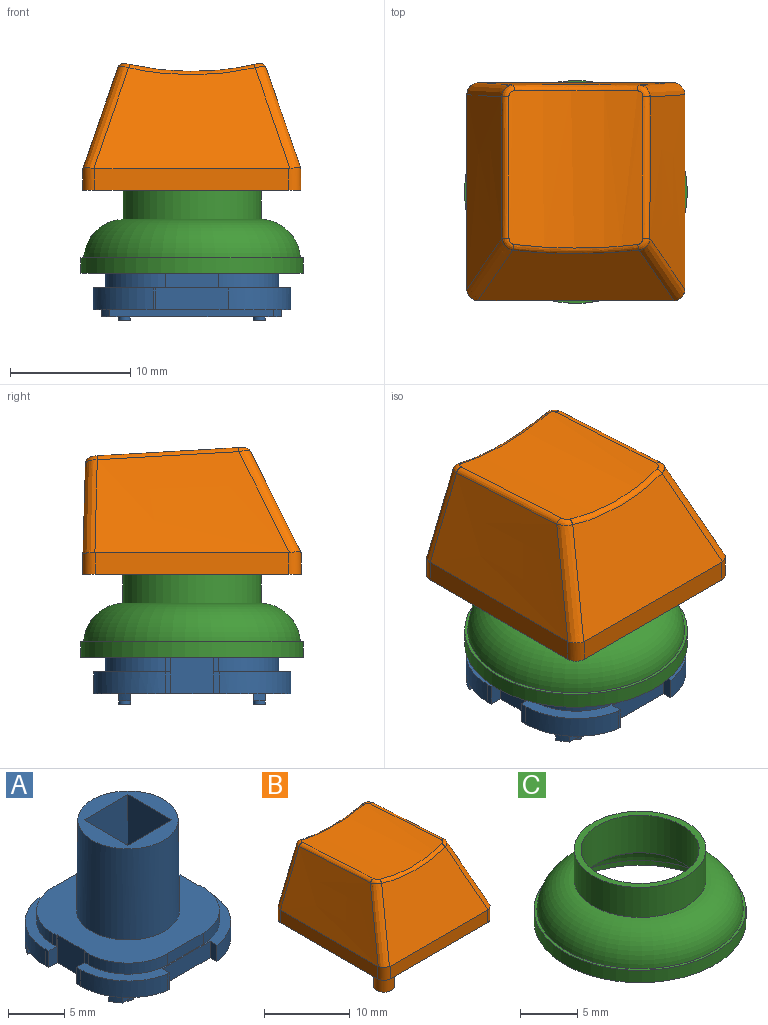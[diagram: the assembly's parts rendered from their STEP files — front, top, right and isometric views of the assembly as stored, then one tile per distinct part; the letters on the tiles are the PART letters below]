
ASSEMBLY  parts=3 mates=2
PART A: 86 faces, bbox 16.4x16.4x13.7 mm
  f0: plane 6x1.8mm, normal (0,1,0), area 10.8mm2, adj f3,f10,f11,f12
  f1: plane 1x1mm, normal (0,0,-1), area 0.8mm2, adj f13
  f2: plane 1x1mm, normal (0,0,-1), area 0.8mm2, adj f14
  f3: plane 1.8x0.85mm, normal (1,0,0), area 1.5mm2, adj f0,f11,f12,f26
  f4: plane 1.2x0.45mm, normal (-1,0,0), area 0.5mm2, adj f5,f11,f27,f28
  f5: revolved ~5x5mm, area 9.4mm2, adj f4,f6,f11,f28
  f6: plane 4.4x1.2mm, normal (0,1,0), area 5.3mm2, adj f5,f7,f11,f28
  f7: revolved ~5x5mm, area 9.4mm2, adj f6,f9,f11,f28
  f8: revolved ~9.8x9.13mm, area 277.6mm2, adj f19,f28
  f9: plane 1.2x0.45mm, normal (1,0,0), area 0.5mm2, adj f7,f11,f28,f29
  f10: plane 1.8x0.85mm, normal (-1,0,0), area 1.5mm2, adj f0,f11,f12,f31
  f11: plane 16.4x6.4mm, normal (0,0,1), area 17.2mm2, adj f0,f3,f4,f5,f6,f7,f9,f10
  f12: plane 13.52x2.05mm, normal (0,0,-1), area 17.2mm2, adj f0,f3,f10,f15,f26,f31
  f13: revolved ~1x1mm, area 0.9mm2, adj f1,f32,f33
  f14: revolved ~1x1mm, area 0.9mm2, adj f2,f33,f34
  f15: plane 13.52x0.6mm, normal (0,1,0), area 8.1mm2, adj f12,f32,f33,f34,f35,f36
  f16: plane 2.8x0.75mm, normal (0,0,-1), area 2.1mm2, adj f40,f41,f42,f43
  f17: plane 2.8x0.75mm, normal (0,0,-1), area 2.1mm2, adj f44,f45,f46,f47
  f18: plane 2.8x0.75mm, normal (0,0,-1), area 2.1mm2, adj f48,f49,f50,f51
  f19: plane 8.9x8.9mm, normal (0,0,1), area 32mm2, adj f8,f43,f47,f51,f52
  f20: plane 2.8x0.75mm, normal (0,0,-1), area 2.1mm2, adj f37,f38,f39,f52
  f21: revolved ~5x5mm, area 9.4mm2, adj f22,f24,f28,f55
  f22: plane 4.4x1.2mm, normal (0,-1,0), area 5.3mm2, adj f21,f23,f28,f55
  f23: revolved ~5x5mm, area 9.4mm2, adj f22,f28,f53,f55
  f24: plane 1.2x0.45mm, normal (1,0,0), area 0.5mm2, adj f21,f28,f55,f57
  f25: plane 1.8x0.45mm, normal (-1,0,0), area 0.8mm2, adj f11,f26,f27,f58
  f26: revolved ~5.95x5.2mm, area 15.5mm2, adj f3,f11,f12,f25,f35,f58
  f27: plane 3x1.1mm, normal (0,-1,0), area 2.1mm2, adj f4,f11,f25,f28,f58,f59,f72
  f28: plane 14.4x14.4mm, normal (0,0,1), area 119.7mm2, adj f4,f5,f6,f7,f8,f9,f21,f22
  f29: plane 3x1.1mm, normal (0,-1,0), area 2.1mm2, adj f9,f11,f28,f30,f60,f61,f72
  f30: plane 1.8x0.45mm, normal (1,0,0), area 0.8mm2, adj f11,f29,f31,f61
  f31: revolved ~5.95x5.2mm, area 15.5mm2, adj f10,f11,f12,f30,f36,f61
  f32: plane 1.86x1mm, normal (0,0,-1), area 1.1mm2, adj f13,f15,f36,f62
  f33: plane 11.2x1mm, normal (0,0,-1), area 10.4mm2, adj f13,f14,f15,f62
  f34: plane 1.85x1mm, normal (0,0,-1), area 1.1mm2, adj f14,f15,f35,f62
  f35: revolved ~1x0.69mm, area 0.7mm2, adj f15,f26,f34,f62
  f36: revolved ~1x0.69mm, area 0.7mm2, adj f15,f31,f32,f62
  f37: plane 5.9x0.75mm, normal (0,1,0), area 4.4mm2, adj f20,f38,f52,f63
  f38: plane 5.9x2.8mm, normal (1,0,0), area 16.5mm2, adj f20,f37,f39,f63
  f39: plane 5.9x0.75mm, normal (0,-1,0), area 4.4mm2, adj f20,f38,f52,f63
  f40: plane 5.9x0.75mm, normal (1,0,0), area 4.4mm2, adj f16,f41,f43,f63
  f41: plane 5.9x2.8mm, normal (0,-1,0), area 16.5mm2, adj f16,f40,f42,f63
  f42: plane 5.9x0.75mm, normal (-1,0,0), area 4.4mm2, adj f16,f41,f43,f63
  f43: plane 12.8x5.5mm, normal (0,-1,0), area 53.9mm2, adj f16,f19,f40,f42,f47,f52,f63
  f44: plane 5.9x0.75mm, normal (0,-1,0), area 4.4mm2, adj f17,f45,f47,f63
  f45: plane 5.9x2.8mm, normal (-1,0,0), area 16.5mm2, adj f17,f44,f46,f63
  f46: plane 5.9x0.75mm, normal (0,1,0), area 4.4mm2, adj f17,f45,f47,f63
  f47: plane 12.8x5.5mm, normal (-1,0,0), area 53.9mm2, adj f17,f19,f43,f44,f46,f51,f63
  f48: plane 5.9x0.75mm, normal (-1,0,0), area 4.4mm2, adj f18,f49,f51,f63
  f49: plane 5.9x2.8mm, normal (0,1,0), area 16.5mm2, adj f18,f48,f50,f63
  f50: plane 5.9x0.75mm, normal (1,0,0), area 4.4mm2, adj f18,f49,f51,f63
  f51: plane 12.8x5.5mm, normal (0,1,0), area 53.9mm2, adj f18,f19,f47,f48,f50,f52,f63
  f52: plane 12.8x5.5mm, normal (1,0,0), area 53.9mm2, adj f19,f20,f37,f39,f43,f51,f63
  f53: plane 1.2x0.45mm, normal (-1,0,0), area 0.5mm2, adj f23,f28,f55,f64
  f54: plane 1.8x0.2mm, normal (0,-1,0), area 0.4mm2, adj f55,f66,f70,f77
  f55: plane 16.4x6.45mm, normal (0,0,1), area 17.6mm2, adj f21,f22,f23,f24,f53,f54,f56,f57
  f56: plane 1.8x0.45mm, normal (1,0,0), area 0.8mm2, adj f55,f57,f69,f71
  f57: plane 3x1.1mm, normal (0,1,0), area 2.1mm2, adj f24,f28,f55,f56,f60,f71,f72
  f58: plane 3.35x1.93mm, normal (0,0,-1), area 3.5mm2, adj f25,f26,f27,f62,f72
  f59: plane 3.5x3mm, normal (-1,0,0), area 10.5mm2, adj f27,f28,f64,f72
  f60: plane 3.5x3mm, normal (1,0,0), area 10.5mm2, adj f28,f29,f57,f72
  f61: plane 3.35x1.93mm, normal (0,0,-1), area 3.5mm2, adj f29,f30,f31,f62,f72
  f62: plane 14.91x0.6mm, normal (0,-1,0), area 8.9mm2, adj f32,f33,f34,f35,f36,f58,f61,f72
  f63: plane 9.2x9.2mm, normal (0,0,-1), area 27.8mm2, adj f37,f38,f39,f40,f41,f42,f43,f44
  f64: plane 3x1.1mm, normal (0,1,0), area 2.1mm2, adj f28,f53,f55,f59,f65,f72,f73
  f65: plane 1.8x0.53mm, normal (-1,0,0), area 1mm2, adj f55,f64,f70,f73
  f66: plane 1.8x0.9mm, normal (1,0,0), area 1.6mm2, adj f54,f55,f67,f77
  f67: plane 6x1.8mm, normal (0,-1,0), area 10.8mm2, adj f55,f66,f68,f77
  f68: plane 1.8x0.85mm, normal (-1,0,0), area 1.5mm2, adj f55,f67,f69,f77
  f69: revolved ~5.95x5.2mm, area 15.5mm2, adj f55,f56,f68,f71,f75,f77
  f70: revolved ~5.92x5mm, area 15.2mm2, adj f54,f55,f65,f73,f77,f78
  f71: plane 3.35x1.93mm, normal (0,0,-1), area 3.5mm2, adj f56,f57,f69,f72,f79
  f72: plane 14.4x10.2mm, normal (0,0,-1), area 76.3mm2, adj f27,f29,f57,f58,f59,f60,f61,f62
  f73: plane 3.35x1.93mm, normal (0,0,-1), area 3.6mm2, adj f64,f65,f70,f72,f79
  f74: plane 1x1mm, normal (0,0,-1), area 0.8mm2, adj f80
  f75: revolved ~1x0.69mm, area 0.7mm2, adj f69,f76,f79,f81
  f76: plane 1.86x1mm, normal (0,0,-1), area 1.1mm2, adj f75,f79,f80,f81
  f77: plane 13.59x2.1mm, normal (0,0,-1), area 17.5mm2, adj f54,f66,f67,f68,f69,f70,f81
  f78: revolved ~1x0.67mm, area 0.7mm2, adj f70,f79,f81,f82
  f79: plane 14.95x0.6mm, normal (0,1,0), area 9mm2, adj f71,f72,f73,f75,f76,f78,f82,f83
  f80: revolved ~1x1mm, area 0.9mm2, adj f74,f76,f83
  f81: plane 13.59x0.6mm, normal (0,-1,0), area 8.2mm2, adj f75,f76,f77,f78,f82,f83
  f82: plane 1.9x1mm, normal (0,0,-1), area 1.2mm2, adj f78,f79,f81,f84
  f83: plane 11.2x1mm, normal (0,0,-1), area 10.4mm2, adj f79,f80,f81,f84
  f84: revolved ~1x1mm, area 0.9mm2, adj f82,f83,f85
  f85: plane 1x1mm, normal (0,0,-1), area 0.8mm2, adj f84
PART B: 42 faces, bbox 21.7x23.1x23.9 mm
  f0: plane 18.1x18.1mm, normal (0,0,-1), area 67.5mm2, adj f1,f2,f3,f4,f10,f12,f14,f16
  f1: plane 16.1x1.8mm, normal (1,0,0), area 29mm2, adj f0,f8,f10,f16
  f2: plane 16.11x1.81mm, normal (0,1,0), area 29mm2, adj f0,f5,f14,f15,f16,f17
  f3: plane 16.1x1.8mm, normal (-1,0,0), area 29mm2, adj f0,f6,f12,f14
  f4: plane 16.1x1.8mm, normal (0,-1,0), area 29mm2, adj f0,f7,f10,f12
  f5: plane 15.98x7.41mm, normal (0,1,0.03), area 93.8mm2, adj f2,f15,f17,f20
  f6: bspline ~18.1x8.87mm, area 120mm2, adj f3,f12,f13,f14,f15,f19
  f7: plane 16.29x8.38mm, normal (0,-0.89,0.45), area 120.9mm2, adj f4,f10,f11,f12,f13,f23
  f8: bspline ~18.1x8.87mm, area 120mm2, adj f1,f10,f11,f16,f17,f24
  f9: cylinder r=22.9mm len=12.8mm, axis (0,1,-0.06), area 143.2mm2, adj f18,f19,f20,f21,f22,f23,f24,f25
  f10: cylinder r=1mm len=1.87mm, axis (0,0,-1), area 2.9mm2, adj f0,f1,f4,f7,f8,f11
  f11: bspline ~10.73x6.1mm, area 14mm2, adj f7,f8,f10,f25
  f12: cylinder r=1mm len=1.87mm, axis (0,0,1), area 2.9mm2, adj f0,f3,f4,f6,f7,f13
  f13: bspline ~10.73x6.1mm, area 14mm2, adj f6,f7,f12,f21
  f14: cylinder r=1mm len=1.8mm, axis (0,0,-1), area 2.8mm2, adj f0,f2,f3,f6,f15
  f15: bspline ~12.92x5.65mm, area 12.7mm2, adj f2,f5,f6,f14,f18
  f16: cylinder r=1mm len=1.8mm, axis (0,0,1), area 2.8mm2, adj f0,f1,f2,f8,f17
  f17: bspline ~12.92x5.65mm, area 12.7mm2, adj f2,f5,f8,f16,f22
  f18: bspline ~1.21x1.1mm, area 0.9mm2, adj f9,f15,f19,f20
  f19: bspline ~18.69x1.5mm, area 8.7mm2, adj f6,f9,f18,f21
  f20: bspline ~10.43x1.06mm, area 7.7mm2, adj f5,f9,f18,f22
  f21: bspline ~1.16x1.07mm, area 0.7mm2, adj f9,f13,f19,f23
  f22: bspline ~1.26x1.04mm, area 0.9mm2, adj f9,f17,f20,f24
  f23: bspline ~10.5x0.84mm, area 6.1mm2, adj f7,f9,f21,f25
  f24: bspline ~18.69x1.5mm, area 8.7mm2, adj f8,f9,f22,f25
  f25: bspline ~1.25x1.04mm, area 0.7mm2, adj f9,f11,f23,f24
  f26: plane 16.11x1.64mm, normal (-1,0,0), area 26.2mm2, adj f0,f27,f29,f32,f33
  f27: plane 16.1x1.79mm, normal (0,-1,0), area 28.7mm2, adj f0,f26,f28,f30,f31,f33
  f28: plane 16.11x1.64mm, normal (1,0,0), area 26.2mm2, adj f0,f27,f29,f31,f32
  f29: plane 16.1x1.56mm, normal (0,1,0), area 25.2mm2, adj f0,f26,f28,f32
  f30: plane 16.08x7.07mm, normal (0,-1,-0.03), area 88.7mm2, adj f27,f31,f33,f34
  f31: offset ~20.1x10.87mm, area 111.8mm2, adj f27,f28,f30,f32,f34
  f32: plane 16.62x8.4mm, normal (0,0.89,-0.45), area 113.5mm2, adj f26,f28,f29,f31,f33,f34
  f33: offset ~20.1x10.87mm, area 111.8mm2, adj f26,f27,f30,f32,f34
  f34: cylinder r=23.9mm len=12.01mm, axis (0,1,-0.06), area 101.5mm2, adj f30,f31,f32,f33,f36,f37,f38,f39
  f35: plane 5.3x5.3mm, normal (0,0,-1), area 23.6mm2, adj f36,f37,f38,f39,f40
  f36: plane 14.71x5.32mm, normal (0,1,0), area 77.3mm2, adj f34,f35,f37,f38
  f37: plane 15x5.3mm, normal (1,0,0), area 78.7mm2, adj f34,f35,f36,f39
  f38: plane 15x5.3mm, normal (-1,0,0), area 78.7mm2, adj f34,f35,f36,f39
  f39: plane 15.02x5.32mm, normal (0,-1,0), area 79mm2, adj f34,f35,f37,f38
  f40: cylinder r=1.2mm len=3.5mm, axis (0,0,1), area 26.4mm2, adj f35,f41
  f41: plane 2.4x2.4mm, normal (0,0,-1), area 4.5mm2, adj f40
PART C: 9 faces, bbox 19.5x19.5x7.7 mm
  f0: cylinder r=9.25mm len=18.5mm, axis (0,0,1), area 76.2mm2, adj f1,f8
  f1: plane 18.5x18.5mm, normal (0,0,-1), area 41.8mm2, adj f0,f2
  f2: cylinder r=8.5mm len=17mm, axis (0,0,1), area 27.5mm2, adj f1,f3
  f3: torus R=5.16mm, axis (0,0,1), area 232.3mm2, adj f2,f4
  f4: cylinder r=5.15mm len=10.3mm, axis (0,0,1), area 129.4mm2, adj f3,f5
  f5: plane 11.5x11.5mm, normal (0,0,1), area 20.5mm2, adj f4,f6
  f6: cylinder r=5.75mm len=11.5mm, axis (0,0,1), area 115.6mm2, adj f5,f7
  f7: torus R=5.6mm, axis (0,0,1), area 243.6mm2, adj f6,f8
  f8: plane 18.5x18.5mm, normal (0,0,1), area 14.3mm2, adj f0,f7
PLACE A at identity fixed
PLACE B t=(0,0,9.9)mm
PLACE C t=(0,0,3)mm
MATE fastened A.f19 <-> B.f40  axis (0,0,1) through (0,0,12.8)mm
MATE fastened A.f28 <-> C.f0  axis (0,0,1) through (0,0,3)mm
